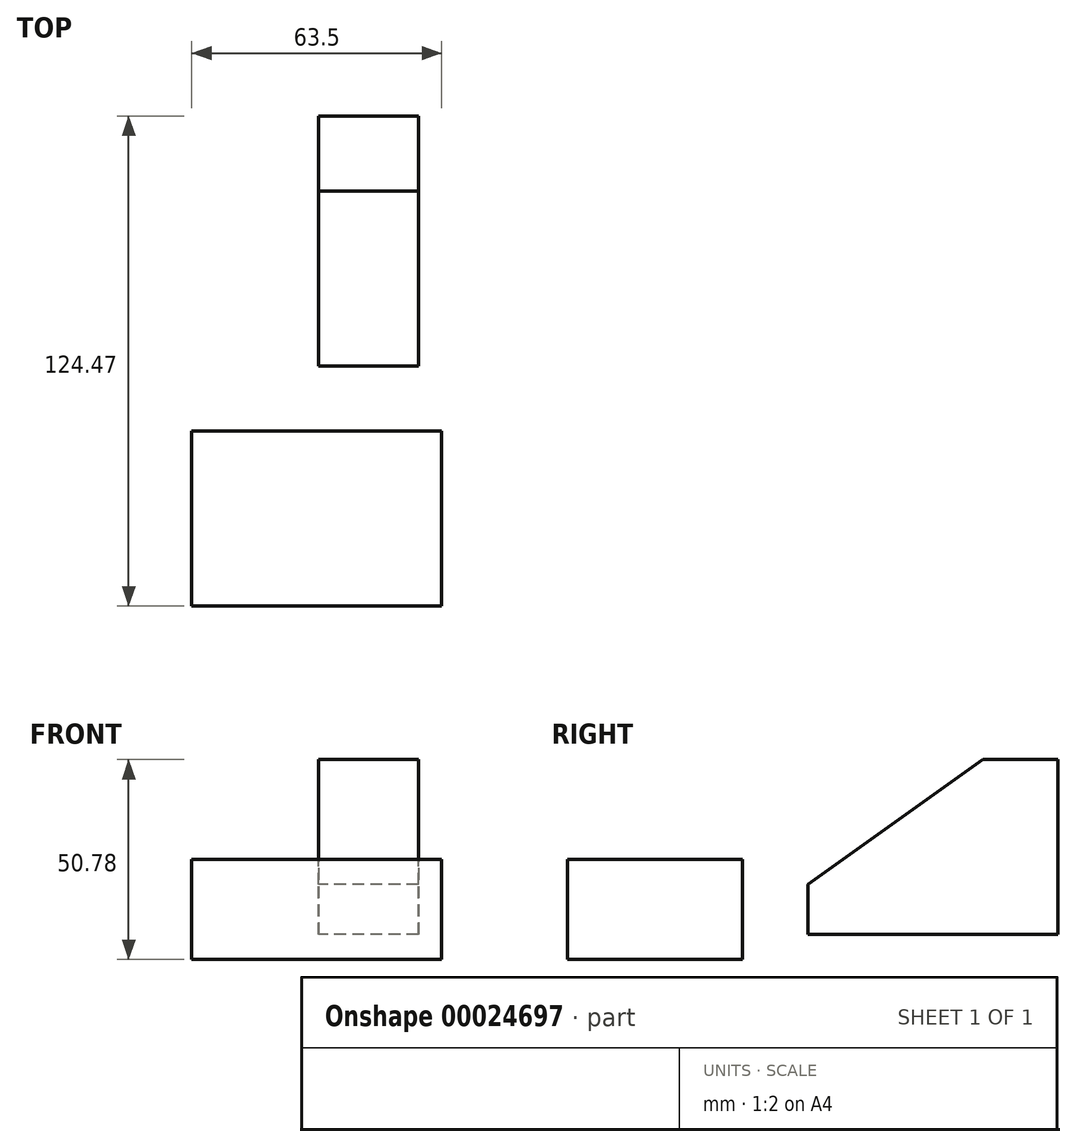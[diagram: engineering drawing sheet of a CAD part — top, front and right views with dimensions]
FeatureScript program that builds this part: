
annotation { "Feature Type Name" : "Feature", "Feature Type Description" : "" }
export const myFeature = defineFeature(function(context is Context, id is Id, definition is map)
    precondition{}
    {
        {
            var Q0;
            Q0=qCreatedBy(makeId("Top.planeOp"),FACE);
            var sketch = newSketch(context, id + "F0", { "sketchPlane" : qUnion([Q0])});
            skLineSegment(sketch, "E0.bottom", {"start": v(-32.19, 20.38) * mm, "end": v(31.31, 20.38) * mm});
            skLineSegment(sketch, "E0.top", {"start": v(-32.19, -24.07) * mm, "end": v(31.31, -24.07) * mm});
            skLineSegment(sketch, "E0.left", {"start": v(-32.19, 20.38) * mm, "end": v(-32.19, -24.07) * mm});
            skLineSegment(sketch, "E0.right", {"start": v(31.31, 20.38) * mm, "end": v(31.31, -24.07) * mm});
            skSolve(sketch);
        }
        {
            var Q0;
            Q0 = qSketchRegion(id + "F0", true);
            extrude(context, id + "F1", {"entities" : qUnion([Q0]), "depth" : 25.4 * mm});
        }
        {
            var Q0;
            Q0=qCreatedBy(makeId("Right.planeOp"),FACE);
            var sketch = newSketch(context, id + "F2", { "sketchPlane" : qUnion([Q0])});
            skLineSegment(sketch, "E1", {"start": v(81.35, 50.78) * mm, "end": v(100.4, 50.78) * mm});
            skLineSegment(sketch, "E2", {"start": v(100.4, 50.78) * mm, "end": v(100.4, 6.33) * mm});
            skLineSegment(sketch, "E3", {"start": v(100.4, 6.33) * mm, "end": v(36.9, 6.33) * mm});
            skLineSegment(sketch, "E4", {"start": v(36.9, 6.33) * mm, "end": v(36.9, 19.03) * mm});
            skLineSegment(sketch, "E5", {"start": v(36.9, 19.03) * mm, "end": v(81.35, 50.78) * mm});
            skSolve(sketch);
        }
        {
            var Q0;
            Q0=makeQuery(id+"F2.imprint","IMPRINT",FACE,{"disambiguationData":[TD([[makeQuery(id+"F2.imprint","IMPRINT",EDGE,{"derivedFrom":sQuery(id+"F2.wireOp",EDGE,"E1")}),-1.0]])]});
            extrude(context, id + "F3", {"entities" : qUnion([Q0]), "depth" : 25.4 * mm});
        }
    });
